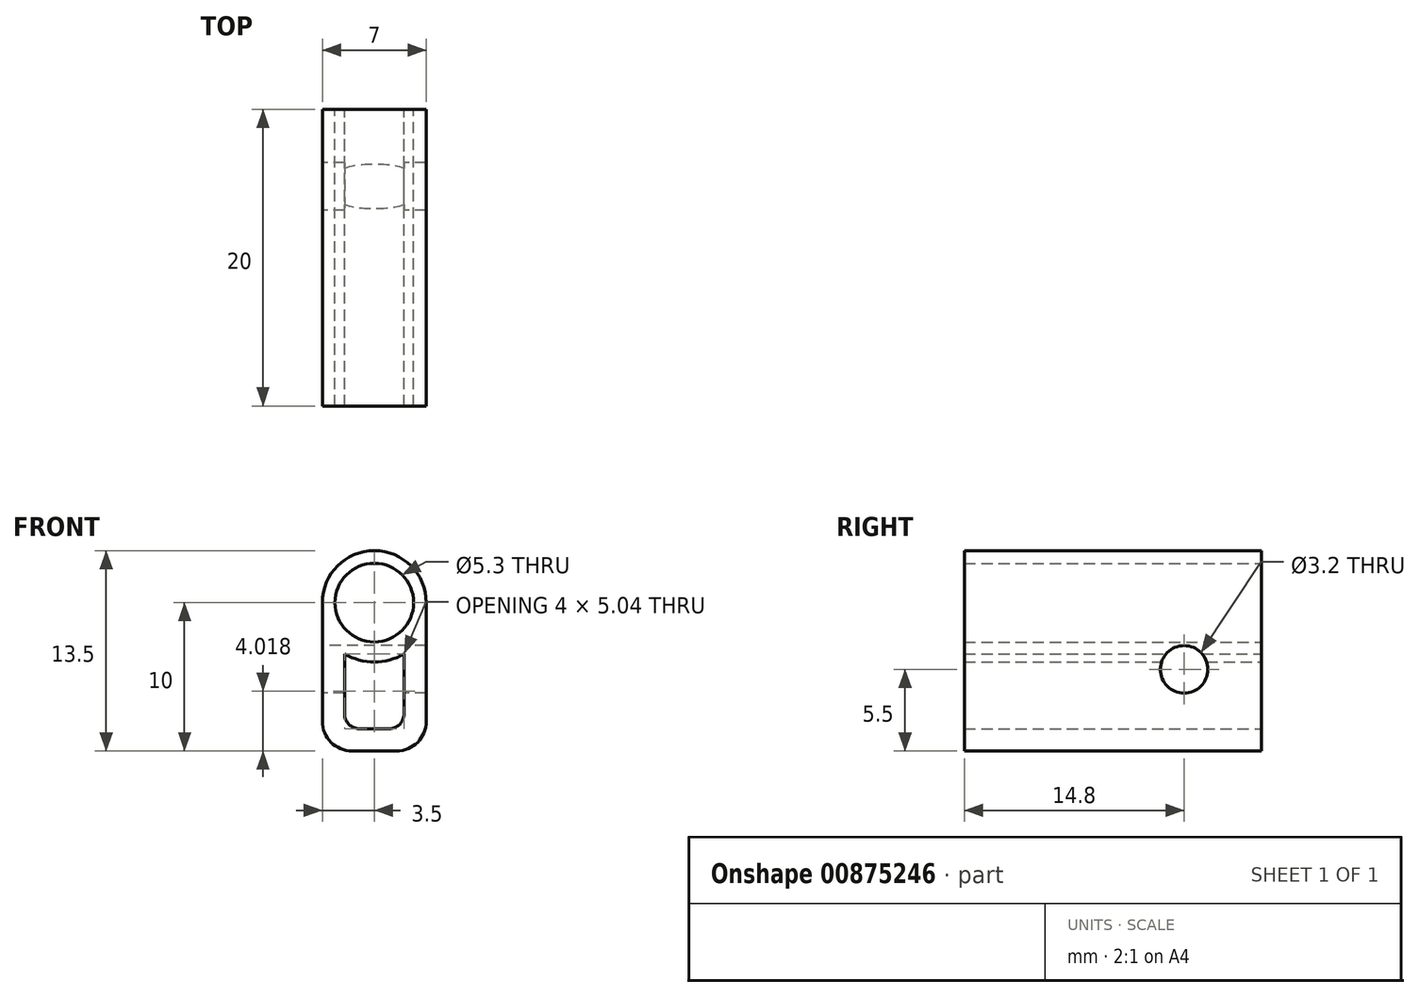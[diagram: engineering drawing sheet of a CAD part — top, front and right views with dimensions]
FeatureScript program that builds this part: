
annotation { "Feature Type Name" : "Feature", "Feature Type Description" : "" }
export const myFeature = defineFeature(function(context is Context, id is Id, definition is map)
    precondition{}
    {
        {
            var Q0;
            Q0=qCreatedBy(makeId("Front.planeOp"),FACE);
            var sketch = newSketch(context, id + "F0", { "sketchPlane" : qUnion([Q0])});
            skArc(sketch, "E0", {"start": v(3.5, 0) * mm, "mid": v(0, 3.5) * mm, "end": v(-3.5, 0) * mm});
            skLineSegment(sketch, "E1", {"start": v(-3.5, 0) * mm, "end": v(-3.5, -10) * mm});
            skLineSegment(sketch, "E2", {"start": v(-3.5, -10) * mm, "end": v(3.5, -10) * mm});
            skLineSegment(sketch, "E3", {"start": v(3.5, -10) * mm, "end": v(3.5, 0) * mm});
            skPoint(sketch, "E4.orphan", {"position": v(2, 0) * mm});
            skLineSegment(sketch, "E5", {"start": v(0, -8.5) * mm, "end": v(0, 0) * mm, "construction": true});
            skSolve(sketch);
        }
        {
            var Q0;
            Q0 = qSketchRegion(id + "F0", true);
            extrude(context, id + "F1", {"entities" : qUnion([Q0]), "depth" : 20 * mm, "offsetDistance" : 25 * mm});
        }
        {
            var Q0;
            Q0=makeQuery(id+"F1.opExtrude","CAP_FACE",FACE,{"disambiguationData":[OSD([sQuery(id+"F0.wireOp",EDGE,"E0"),sQuery(id+"F0.wireOp",EDGE,"E1"),sQuery(id+"F0.wireOp",EDGE,"E2"),sQuery(id+"F0.wireOp",EDGE,"E3")])],"isStart":true});
            var sketch = newSketch(context, id + "F2", { "sketchPlane" : qUnion([Q0])});
            skCircle(sketch, "E6", {"center": v(0, 0) * mm, "radius": 2.65 * mm});
            skArc(sketch, "E7", {"start": v(-2, -3.46) * mm, "mid": v(0, -4) * mm, "end": v(2, -3.46) * mm});
            skLineSegment(sketch, "E8", {"start": v(-2, -3.46) * mm, "end": v(-2, -8.5) * mm});
            skLineSegment(sketch, "E9", {"start": v(-2, -8.5) * mm, "end": v(2, -8.5) * mm});
            skLineSegment(sketch, "E10", {"start": v(2, -8.5) * mm, "end": v(2, -3.46) * mm});
            skLineSegment(sketch, "E11", {"start": v(0, 0) * mm, "end": v(0, -8.5) * mm, "construction": true});
            skPoint(sketch, "E12", {"position": v(0, -10) * mm});
            skSolve(sketch);
        }
        {
            var Q0;
            Q0 = qSketchRegion(id + "F2", true);
            extrude(context, id + "F3", {"entities" : qUnion([Q0]), "operationType" : NewBodyOperationType.REMOVE, "endBound" : BoundingType.THROUGH_ALL, "oppositeDirection" : true, "depth" : 25 * mm, "offsetDistance" : 25 * mm});
        }
        {
            var Q0;
            Q0=makeQuery(id+"F1.opExtrude","SWEPT_FACE",FACE,{"disambiguationData":[OSD([sQuery(id+"F0.wireOp",EDGE,"E1")])]});
            var sketch = newSketch(context, id + "F4", { "sketchPlane" : qUnion([Q0])});
            skCircle(sketch, "E13", {"center": v(5.2, -4.5) * mm, "radius": 1.6 * mm});
            skSolve(sketch);
        }
        {
            var Q0;
            Q0 = qSketchRegion(id + "F4", true);
            extrude(context, id + "F5", {"entities" : qUnion([Q0]), "operationType" : NewBodyOperationType.REMOVE, "endBound" : BoundingType.THROUGH_ALL, "oppositeDirection" : true, "depth" : 25 * mm, "offsetDistance" : 25 * mm});
        }
        {
            var Q0;
            Q0=makeQuery(id+"F1.opExtrude","SWEPT_EDGE",EDGE,{"disambiguationData":[OSD([sQuery(id+"F0.wireOp",EDGE,"E1"),sQuery(id+"F0.wireOp",EDGE,"E2")])]});
            var Q1;
            Q1=makeQuery(id+"F1.opExtrude","SWEPT_EDGE",EDGE,{"disambiguationData":[OSD([sQuery(id+"F0.wireOp",EDGE,"E2"),sQuery(id+"F0.wireOp",EDGE,"E3")])]});
            fillet(context, id + "F6", {"entities" : qUnion([Q0, Q1]), "tangentPropagation" : true, "radius" : 2 * mm, "defaultsChanged" : true, "vertexSettings" : [], "allowEdgeOverflow" : false});
        }
        {
            var Q0;
            Q0=makeQuery(id+"F3.boolean.opBoolean","COPY",EDGE,{"derivedFrom":makeQuery(id+"F3.opExtrude","SWEPT_EDGE",EDGE,{"disambiguationData":[OSD([sQuery(id+"F2.wireOp",EDGE,"E8"),sQuery(id+"F2.wireOp",EDGE,"E9")])]})});
            var Q1;
            Q1=makeQuery(id+"F3.boolean.opBoolean","COPY",EDGE,{"derivedFrom":makeQuery(id+"F3.opExtrude","SWEPT_EDGE",EDGE,{"disambiguationData":[OSD([sQuery(id+"F2.wireOp",EDGE,"E9"),sQuery(id+"F2.wireOp",EDGE,"E10")])]})});
            fillet(context, id + "F7", {"entities" : qUnion([Q0, Q1]), "tangentPropagation" : true, "radius" : 1 * mm, "defaultsChanged" : false, "vertexSettings" : [], "allowEdgeOverflow" : false});
        }
    });
